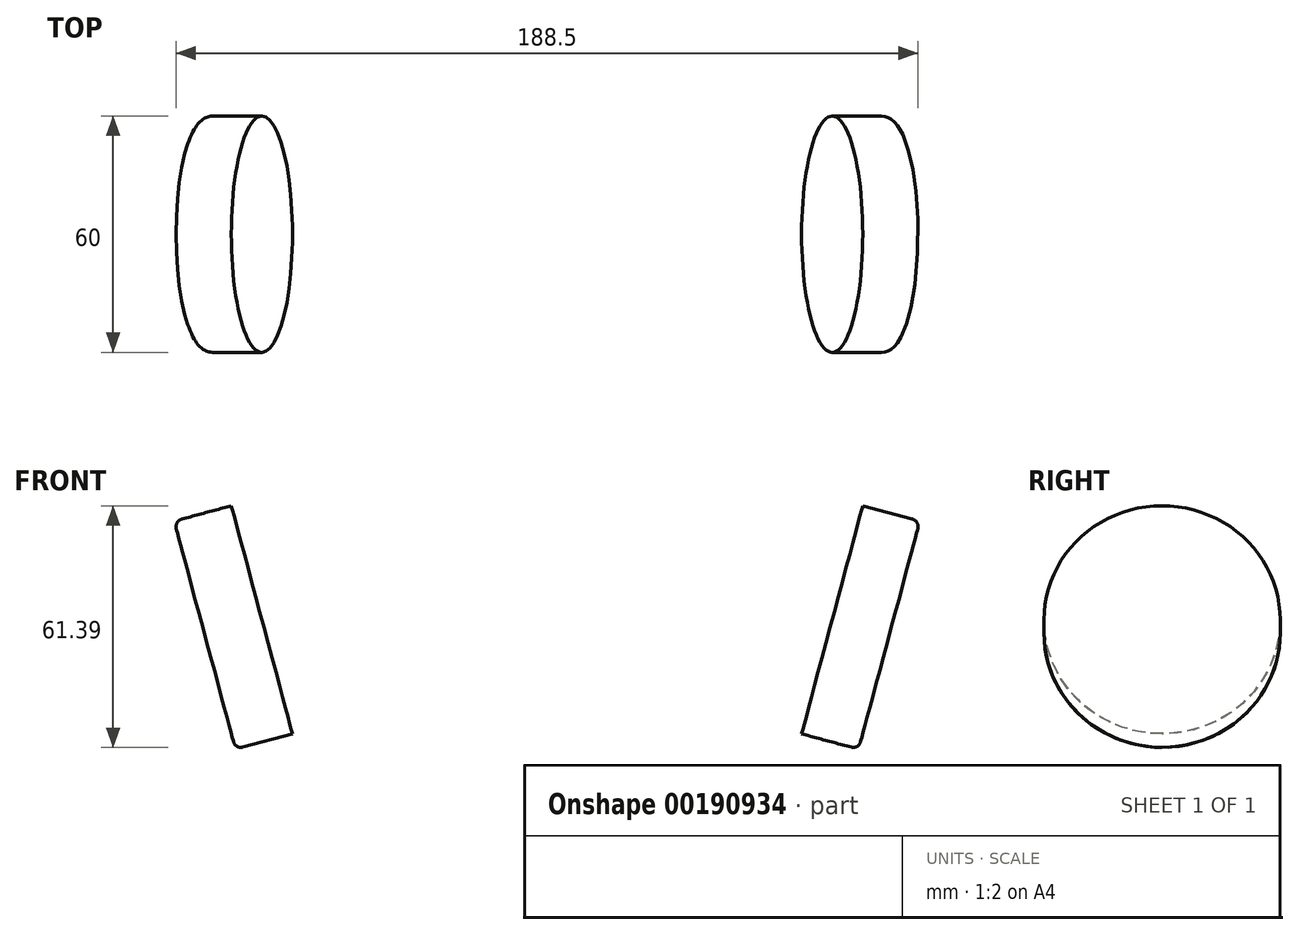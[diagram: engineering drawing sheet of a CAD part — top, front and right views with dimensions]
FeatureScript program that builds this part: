
annotation { "Feature Type Name" : "Feature", "Feature Type Description" : "" }
export const myFeature = defineFeature(function(context is Context, id is Id, definition is map)
    precondition{}
    {
        {
            var Q0;
            Q0=qCreatedBy(makeId("Front.planeOp"),FACE);
            var sketch = newSketch(context, id + "F0", { "sketchPlane" : qUnion([Q0])});
            skArc(sketch, "E0", {"start": v(72.44, -19.41) * mm, "mid": v(0, 75) * mm, "end": v(-72.44, -19.41) * mm});
            skLineSegment(sketch, "E1", {"start": v(-72.44, -19.41) * mm, "end": v(0, 0) * mm, "construction": true});
            skLineSegment(sketch, "E2", {"start": v(72.44, -19.41) * mm, "end": v(0, 0) * mm, "construction": true});
            skLineSegment(sketch, "E3", {"start": v(-80.2, 9.57) * mm, "end": v(-64.68, -48.39) * mm, "construction": true});
            skLineSegment(sketch, "E4", {"start": v(64.68, -48.39) * mm, "end": v(80.2, 9.57) * mm, "construction": true});
            skSolve(sketch);
        }
        {
            var Q0;
            Q0=sQuery(id+"F0.wireOp",EDGE,"E3");
            cPlane(context, id + "F1", {"entities" : qUnion([Q0]), "cplaneType" : CPlaneType.LINE_ANGLE, "offset" : 25 * mm, "angle" : 0 * degree, "width" : 150 * mm, "height" : 150 * mm});
        }
        {
            var Q0;
            Q0=qCreatedBy(id+"F1.planeOp",FACE);
            var sketch = newSketch(context, id + "F2", { "sketchPlane" : qUnion([Q0])});
            skCircle(sketch, "E5", {"center": v(0, 0) * mm, "radius": 30 * mm});
            skSolve(sketch);
        }
        {
            var Q0;
            Q0 = qSketchRegion(id + "F2", true);
            extrude(context, id + "F3", {"entities" : qUnion([Q0]), "depth" : 15 * mm});
        }
        {
            var Q0;
            Q0=makeQuery(id+"F3.opExtrude","SWEPT_BODY",BODY,{"disambiguationData":[OSD([sQuery(id+"F2.wireOp",EDGE,"E5")])]});
            var Q1;
            Q1=qCreatedBy(makeId("Right.planeOp"),FACE);
            mirror(context, id + "F4", {"entities" : qUnion([Q0]), "mirrorPlane" : qUnion([Q1])});
        }
        {
            var Q0;
            Q0=makeQuery(id+"F3.opExtrude","CAP_FACE",FACE,{"disambiguationData":[OSD([sQuery(id+"F2.wireOp",EDGE,"E5")])],"isStart":false});
            var Q1;
            Q1=makeQuery(id+"F4.opPattern","COPY",FACE,{"derivedFrom":makeQuery(id+"F3.opExtrude","CAP_FACE",FACE,{"disambiguationData":[OSD([sQuery(id+"F2.wireOp",EDGE,"E5")])],"isStart":false}),"instanceName":"1"});
            fillet(context, id + "F5", {"entities" : qUnion([Q0, Q1]), "radius" : 2 * mm, "tangentPropagation" : true, "allowEdgeOverflow" : false});
        }
    });
